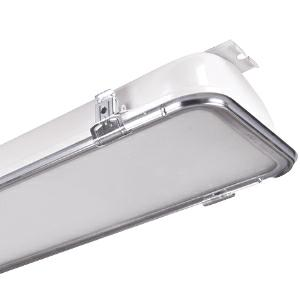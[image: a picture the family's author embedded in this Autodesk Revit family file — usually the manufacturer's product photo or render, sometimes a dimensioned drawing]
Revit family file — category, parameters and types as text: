
# Revit family: 3f_filippi_-_beta_235_76_vs_ampio_3f_filippi_-_52818_-_beta_235_led_762x55_dali_ampio_vs_l1565
name_source: partatom
category: Lighting Fixtures
units: mm (PartAtom-declared; Revit-internal decimal feet)

## family parameters
Cut with Voids When Loaded = No
Host = Face
Light Source = No
Part Type = Normal
Room Calculation Point = No
Round Connector Dimension = Use Diameter
Shared = No

## types (1)
- 3F Filippi - Beta 235 76 VS Ampio (1 x LED, 16005 lm, 112 W, 4000 K)
    Apparent Load = 112 VA
    Approval mark = CE
    CIE Flux Codes = 65 90 98 100 100
    Color Rendering = 80
    Color Temperature = 4000 K
    Control Gear = Electronic transformer
    Default Elevation = 1800 mm
    Description = ILLUMINOTECHNICAL
Luminous efficiency 100% (DLOR 100%, ULOR 0%).
Initial luminous flux of the luminaire 16005 lm.
Wide symmetric distribution.
Installation Interdistance Transv.D = 1.26 x hu - Long.D = 1.32 x hu.
Tabular UGR (CIE 117 - 4H-8H; S=0.25H; 70/50/20): RUG 21.8 - 22.9.
Beam angle: 87° - 92°.
Luminous efficacy 143 lm/W.
Lifetime (L93/B10): 30000 h. (tq+25°C)
Lifetime (L90/B10): 50000 h. (tq+25°C)
Lifetime (L85/B10): 80000 h. (tq+25°C)
Lifetime (L80/B10): 100000 h. (tq+25°C)
Lifetime (L85/B10): 50000 h. (tq+45°C)
Sudden decreased luminous flux after 50000 hours: 0% (C0).
Photobiological safety in compliance with IEC/TR 62778: RG0 risk exempt, (IEC 62471).
In compliance with IEC/EN 62722-2-1 - IEC/EN 62717 standards.

SOURCE
2 linear LED modules 55W/840.
Energy efficiency class (UE 2019/2020 - UE 2019/2015): C.
CIE 13.3 Colour rendering index: CRI >80 (R9 <50%).
IES TM-30 Fidelity Index: Rf = 84 Rg = 95.
CCT nominal colour temperature 4000 K.
Colour initial tolerance (MacAdam): SDCM 3.

MECHANICAL
Single-piece housing in pressed steel, powder-coated in white epoxy-polyester.
VS moulded anti-glare glass, non-combustible, single-piece perimeter frame in galvanised steel.
Ecologic anti-aging injected sealing gasket.
Oversized gear-tray reflector unit in highly reflective white painted hot-galvanised steel.
Methacrylate (PMMA) lenses with external flat surface.
Galvanised steel snap-lock clips for diffuser mounting (safety n° 4 per fixture).
Luminaire with limited surface temperature. - D - (EN 60598-2-24)
Dimensions: 1565x235 mm, height 105 mm. Weight 12.22 kg.
IP66 protection degree.
Mechanical strength to impacts IK09 (10 joule).
Glow-wire test resistance 960°C.

ELECTRICAL
Halogen Free DALI-2 DATI (Parts 251, 252, 253), PUSH-DIM, electronic wiring 230V-50/60Hz, power factor 0.95 at full load, THD <25%, constant output current, class I, 1 driver, 1 DALI addresse.
Power of the luminaire 112 W.
ENEC - CE.
SAFE FLICKER: PstLM=<1 and SVM=<0.4 (IEC TR 61547-1 and IEC TR 63158), to ensure a more comfortable and safe light.
Luminaire compliant with EN 60598-2-22 for power supply from a centralised emergency system CPSS (Central Power Supply System), not incorporated in the luminaire - high risk areas excluded. The default power and flux are 100% in AC and 15% in DC.
Ambient temperature from -20°C to +45°C.
Temperature class T6 max 85°C.
Quick connection via M25 5P connector with 9-13 mm tightening range.
Relative humidity UR: <85%.

INSTALLATION
Ceiling / Suspended / Wall.
All accessories dedicated to this product are available on the Catalog and on our website www.3F-Filippi.com.

APPLICATIONS
Dry, dusty indoor environments, subject to occasional water splashes.
Industrial environments, warehouses, environments where security locks are required on all clips, e.g. prisons (on request).
Environments in which it is necessary a total protection against falling fragments (eg environments with foodstuffs or machines with moving parts or with extreme temperature changes), use luminaires with laminated glass.
Tempered glass is not immune to falling fragments from harmless and caused by shocks or exceptionally derived from the tempering process.

LIGHT MANAGEMENT
Recommended minimum setting: 10%.
The luminaire, equipped with (DALI-2 DATI) driver, can be controlled manually with 3F Easy Dim technology or automatically/manually with wired or wireless DALI/D2D control systems.
The D2D driver guarantees interoperability with other devices with the same certification by making the following information available:
Device Data (Part 251), Energy Report (Part 252), Diagnosis & Maintenance (Part 253).
In electrical systems without a regulation system (manual or automatic) and DALI bus, a suitable jumper must be made on the DA-DA terminals of the appliance.

WARNING
Fixture not suitable for cold stores with an ambient temperature <0°C and/or relative humidity >85%.
Luminaire designed for disposal/recycling at end-of-life.
Replaceable (LED only) light source by a professional. Replaceable control gear by a professional.
    Height = 105 mm
    Lamp = 1 x LED
    Lamp Light Flux = 16005 lm
    Lamp Power = 112 W
    Lamp count = 1
    Length = 1565 mm
    Lifetime = 50000 h
    Luminous efficacy = 143 lm/W
    Manufacturer = 3F Filippi
    ModVariant = No
    Model = 3F Filippi - 52818 - Beta 235 LED 762x55 DALI AMPIO VS L1565
    Mounting Place = Ceiling
    Mounting Type = Pendant
    Number of Poles = 1
    OnlyDefault = Yes
    Power Factor = 1
    Product Name = 3F Filippi - Beta 235 76 VS Ampio
    Product group = pendant luminaire
    ProductGroupID = 9
    Protection Class = Protection class I
    Protection Degree = IP 66
    RLX_Detail_Level = 1
    RLX_Emergency_Light_Flux = 0 lm
    RLX_Emergency_Type = 0
    RLX_Emergency_Type_DB = No
    RlxData = <blob elided: 83393 chars, md5=9e0fe80e>
    Socket = socket
    Standby Power = 0 W
    System Light Flux = 16005 lm
    System Power = 112 W
    Type Comments = Product without accessories
    Type Image = 3ffilippi_52818.jpg
    URL = http://relux.com
    VarID = ---
    Voltage = 0 V
    Weight = 0.00 kg
    Width = 235 mm

## geometry (parser evidence)
native form markers: Blend x4, Sweep x11
no freeform markers — native parametric forms only
